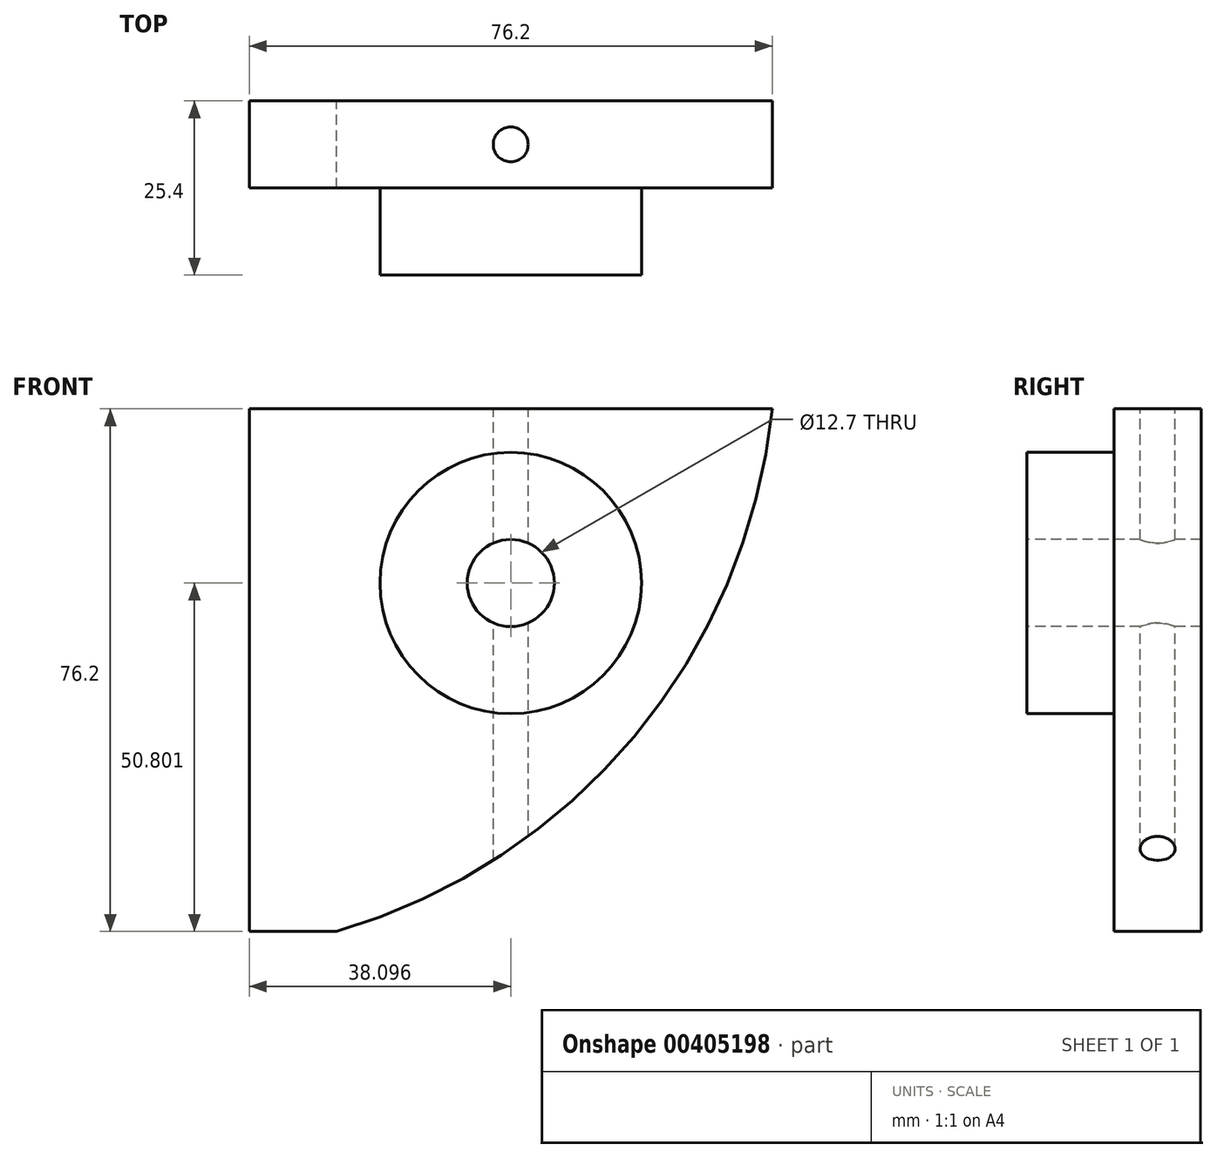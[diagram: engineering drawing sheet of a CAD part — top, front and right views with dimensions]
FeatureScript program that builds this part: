
annotation { "Feature Type Name" : "Feature", "Feature Type Description" : "" }
export const myFeature = defineFeature(function(context is Context, id is Id, definition is map)
    precondition{}
    {
        {
            var Q0;
            Q0=qCreatedBy(makeId("Front.planeOp"),FACE);
            var sketch = newSketch(context, id + "F0", { "sketchPlane" : qUnion([Q0])});
            skLineSegment(sketch, "E0", {"start": v(-73.68, 58.73) * mm, "end": v(2.52, 58.73) * mm});
            skLineSegment(sketch, "E1", {"start": v(-73.68, 58.73) * mm, "end": v(-73.68, -17.47) * mm});
            skLineSegment(sketch, "E2", {"start": v(-73.68, -17.47) * mm, "end": v(-60.98, -17.47) * mm});
            skArc(sketch, "E3", {"start": v(-60.98, -17.47) * mm, "mid": v(-17.62, 10.95) * mm, "end": v(2.52, 58.73) * mm});
            skSolve(sketch);
        }
        {
            var Q0;
            Q0=makeQuery(id+"F0.imprint","IMPRINT",FACE,{"disambiguationData":[TD([[makeQuery(id+"F0.imprint","IMPRINT",EDGE,{"derivedFrom":sQuery(id+"F0.wireOp",EDGE,"E0")}),-1.0]])]});
            extrude(context, id + "F1", {"entities" : qUnion([Q0]), "endBound" : BoundingType.SYMMETRIC, "depth" : 12.7 * mm});
        }
        {
            var Q0;
            Q0=makeQuery(id+"F1.opExtrude","CAP_FACE",FACE,{"disambiguationData":[OSD([sQuery(id+"F0.wireOp",EDGE,"E0"),sQuery(id+"F0.wireOp",EDGE,"E1"),sQuery(id+"F0.wireOp",EDGE,"E2"),sQuery(id+"F0.wireOp",EDGE,"E3")])],"isStart":false});
            var sketch = newSketch(context, id + "F2", { "sketchPlane" : qUnion([Q0])});
            skCircle(sketch, "E4", {"center": v(-35.58, 33.33) * mm, "radius": 19.05 * mm});
            skSolve(sketch);
        }
        {
            var Q0;
            Q0=makeQuery(id+"F2.imprint","IMPRINT",FACE,{"disambiguationData":[TD([[makeQuery(id+"F2.imprint","IMPRINT",EDGE,{"derivedFrom":sQuery(id+"F2.wireOp",EDGE,"E4")}),1.0]])]});
            extrude(context, id + "F3", {"entities" : qUnion([Q0]), "operationType" : NewBodyOperationType.ADD, "depth" : 12.7 * mm});
        }
        {
            var Q0;
            Q0=makeQuery(id+"F3.opExtrude","CAP_FACE",FACE,{"disambiguationData":[OSD([sQuery(id+"F2.wireOp",EDGE,"E4")])],"isStart":false});
            var sketch = newSketch(context, id + "F4", { "sketchPlane" : qUnion([Q0])});
            skCircle(sketch, "E5", {"center": v(-35.58, 33.33) * mm, "radius": 6.35 * mm});
            skSolve(sketch);
        }
        {
            var Q0;
            Q0=makeQuery(id+"F4.imprint","IMPRINT",FACE,{"disambiguationData":[TD([[makeQuery(id+"F4.imprint","IMPRINT",EDGE,{"derivedFrom":sQuery(id+"F4.wireOp",EDGE,"E5")}),1.0]])]});
            extrude(context, id + "F5", {"entities" : qUnion([Q0]), "operationType" : NewBodyOperationType.REMOVE, "oppositeDirection" : true, "depth" : 74.42 * mm});
        }
        {
            var Q0;
            Q0=makeQuery(id+"F1.opExtrude","SWEPT_FACE",FACE,{"disambiguationData":[OSD([sQuery(id+"F0.wireOp",EDGE,"E0")])]});
            var sketch = newSketch(context, id + "F6", { "sketchPlane" : qUnion([Q0])});
            skCircle(sketch, "E6", {"center": v(-35.58, 0) * mm, "radius": 2.54 * mm});
            skSolve(sketch);
        }
        {
            var Q0;
            Q0=makeQuery(id+"F6.imprint","IMPRINT",FACE,{"disambiguationData":[TD([[makeQuery(id+"F6.imprint","IMPRINT",EDGE,{"derivedFrom":sQuery(id+"F6.wireOp",EDGE,"E6")}),1.0]])]});
            extrude(context, id + "F7", {"entities" : qUnion([Q0]), "operationType" : NewBodyOperationType.REMOVE, "endBound" : BoundingType.THROUGH_ALL, "oppositeDirection" : true, "depth" : 25.4 * mm});
        }
    });
